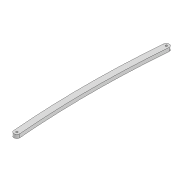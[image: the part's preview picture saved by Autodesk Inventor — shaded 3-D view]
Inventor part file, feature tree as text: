
AUTODESK INVENTOR PART (.ipt)
format: ipt  version: 2022 (Build 260153000, 153)  size: 91,648 bytes
history: native  units: mm
features: extrude x1, sketch x1
ambient origin geometry x8: Origin, YZ Plane, XZ Plane, XY Plane, X Axis, Y Axis, Z Axis, Center Point
bodies: Solid1 (feature_tree)
feature tree (2):
  extrude  "Extrusion1"  Depth=1500.0mm
  sketch  "Sketch1"  dims[d0=3.3mm d1=3.3mm d2=10.0mm d3=253.429mm d6=6.0mm d7=0.0mm d16=1500.0mm d17=1500.0mm]
